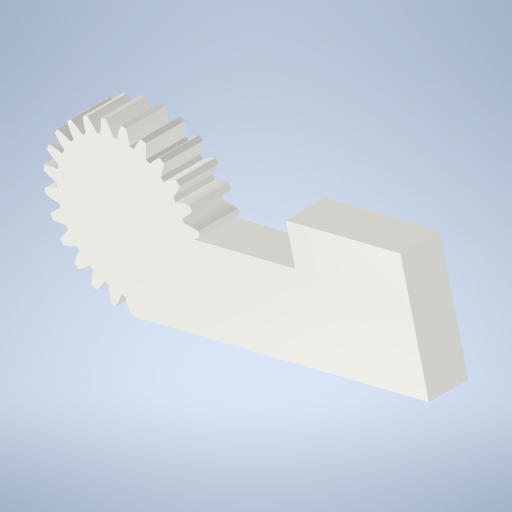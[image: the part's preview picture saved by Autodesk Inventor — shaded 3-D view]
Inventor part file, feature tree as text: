
AUTODESK INVENTOR PART (.ipt)
format: ipt  version: 2024 (Build 280153000, 153)  size: 478,720 bytes
history: native  units: mm (DEFAULTED — no unit token found)
features: plane x3, other x3, extrude x2, sketch x2, projected_geometry x1
ambient origin geometry x8: Origin, YZ Plane, XZ Plane, XY Plane, X Axis, Y Axis, Z Axis, Center Point
bodies: Solid1 (feature_tree)
feature tree (11):
  extrude  "Extrusion1"  Depth=6.666667mm TaperAngle=0.0deg
  plane  "Work Plane2"
  plane  "Work Plane8"
  plane  "Work Plane9"
  other  "Spur Gear"
  extrude  "Extrusion2"  Depth=10.0mm TaperAngle=0.0deg
  sketch  "Sketch1"  dims[d0=27.0mm d1=6.666667mm d2=0.0mm]
  other  "Srf1"
  sketch  "Sketch4"  dims[d3=25.0mm d4=10.0mm d5=0.0mm d16=25.0mm d17=0.0mm d34=1.256637mm d39=0.0mm d41=0.0mm d43=25.0mm d46=25.0mm d47=0.0mm d48=0.0mm d50=20.0mm d51=20.0mm d53=10.0mm d54=0.0mm d59=13.264502mm d60=6.307mm d61=30.0mm d62=90.0deg d63=90.0deg d64=90.0deg d65=50.0mm]
  projected_geometry  "Projected Loop1"
  other  "Pitch Diameter"
